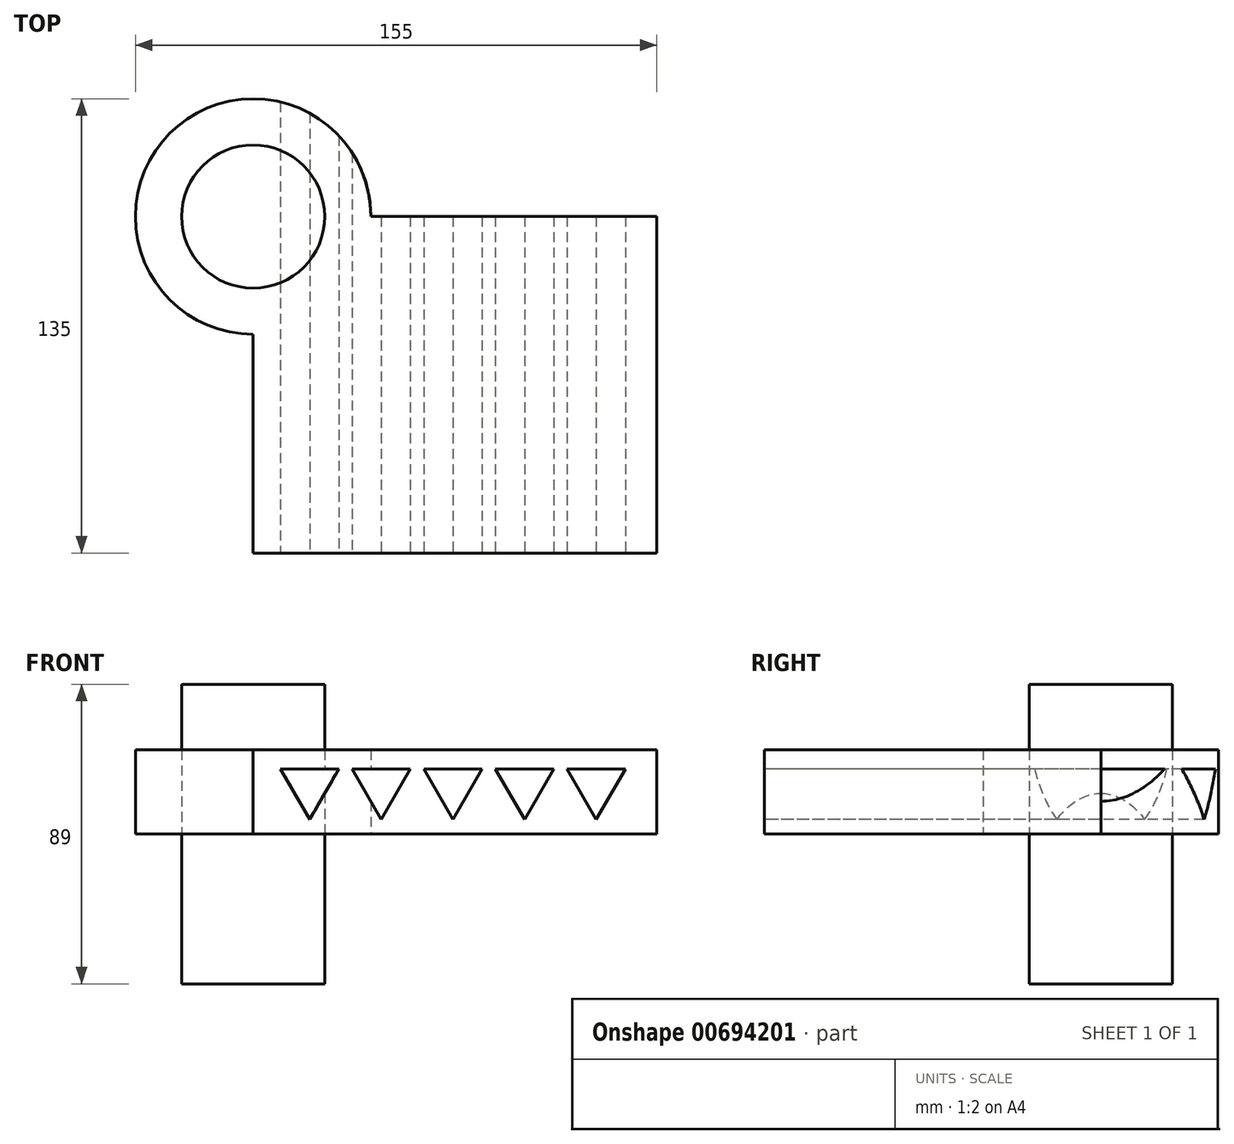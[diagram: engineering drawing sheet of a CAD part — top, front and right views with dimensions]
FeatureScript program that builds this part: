
annotation { "Feature Type Name" : "Feature", "Feature Type Description" : "" }
export const myFeature = defineFeature(function(context is Context, id is Id, definition is map)
    precondition{}
    {
        {
            var Q0;
            Q0=qCreatedBy(makeId("Top.planeOp"),FACE);
            var sketch = newSketch(context, id + "F0", { "sketchPlane" : qUnion([Q0])});
            skLineSegment(sketch, "E0.bottom", {"start": v(60, -50) * mm, "end": v(-60, -50) * mm});
            skLineSegment(sketch, "E0.top", {"start": v(60, 50) * mm, "end": v(-60, 50) * mm});
            skLineSegment(sketch, "E0.left", {"start": v(60, -50) * mm, "end": v(60, 50) * mm});
            skLineSegment(sketch, "E0.right", {"start": v(-60, -50) * mm, "end": v(-60, 50) * mm});
            skPoint(sketch, "E0.middle", {"position": v(0, 0) * mm});
            skCircle(sketch, "E1", {"center": v(-60, 50) * mm, "radius": 35 * mm});
            skArc(sketch, "E2", {"start": v(-41.18, 79.51) * mm, "mid": v(7.3, 57.53) * mm, "end": v(60, 50) * mm});
            skCircle(sketch, "E3", {"center": v(-60, 50) * mm, "radius": 21.28 * mm});
            skSolve(sketch);
        }
        {
            var Q0;
            {var subQ0=sQuery(id+"F0.wireOp",EDGE,"E1");var subQ4=sQuery(id+"F0.wireOp",EDGE,"E0.top");var subQ5=makeQuery(id+"F0.imprint","INTERSECT",VERTEX,{"derivedFrom":[subQ4,subQ0]});Q0=makeQuery(id+"F0.imprint","IMPRINT",FACE,{"disambiguationData":[TD([[makeQuery(id+"F0.imprint","IMPRINT",EDGE,{"disambiguationData":[TD([[subQ5,-1.0]])],"derivedFrom":subQ4}),-1.0]])]});}
            var Q1;
            {var subQ5=sQuery(id+"F0.wireOp",EDGE,"E0.bottom");Q1=makeQuery(id+"F0.imprint","IMPRINT",FACE,{"disambiguationData":[TD([[makeQuery(id+"F0.imprint","IMPRINT",EDGE,{"derivedFrom":subQ5}),-1.0]])]});}
            var Q2;
            {var subQ0=sQuery(id+"F0.wireOp",EDGE,"E1");var subQ1=sQuery(id+"F0.wireOp",EDGE,"E0.top");var subQ2=makeQuery(id+"F0.imprint","INTERSECT",VERTEX,{"derivedFrom":[subQ1,subQ0]});Q2=makeQuery(id+"F0.imprint","IMPRINT",FACE,{"disambiguationData":[TD([[makeQuery(id+"F0.imprint","IMPRINT",EDGE,{"disambiguationData":[TD([[subQ2,-1.0]])],"derivedFrom":subQ1}),1.0]])]});}
            extrude(context, id + "F1", {"entities" : qUnion([Q0, Q1, Q2]), "depth" : 25 * mm, "offsetDistance" : 25 * mm});
        }
        {
            var Q0;
            {var subQ0=sQuery(id+"F0.wireOp",EDGE,"E0.right");var subQ1=sQuery(id+"F0.wireOp",EDGE,"E0.top");var subQ2=makeQuery(id+"F0.imprint","INTERSECT",VERTEX,{"derivedFrom":[subQ1,subQ0]});Q0=makeQuery(id+"F0.imprint","IMPRINT",FACE,{"disambiguationData":[TD([[makeQuery(id+"F0.imprint","IMPRINT",EDGE,{"disambiguationData":[TD([[subQ2,1.0]])],"derivedFrom":subQ1}),-1.0]])]});}
            var Q1;
            {var subQ0=sQuery(id+"F0.wireOp",EDGE,"E0.right");var subQ1=sQuery(id+"F0.wireOp",EDGE,"E0.top");var subQ2=makeQuery(id+"F0.imprint","INTERSECT",VERTEX,{"derivedFrom":[subQ1,subQ0]});Q1=makeQuery(id+"F0.imprint","IMPRINT",FACE,{"disambiguationData":[TD([[makeQuery(id+"F0.imprint","IMPRINT",EDGE,{"disambiguationData":[TD([[subQ2,1.0]])],"derivedFrom":subQ1}),1.0]])]});}
            extrude(context, id + "F2", {"entities" : qUnion([Q0, Q1]), "endBound" : BoundingType.SYMMETRIC, "depth" : 89 * mm, "offsetDistance" : 25 * mm});
        }
        {
            var Q0;
            Q0=makeQuery(id+"F1.opExtrude","SWEPT_FACE",FACE,{"disambiguationData":[OSD([sQuery(id+"F0.wireOp",EDGE,"E0.bottom")])]});
            var sketch = newSketch(context, id + "F3", { "sketchPlane" : qUnion([Q0])});
            skCircle(sketch, "E4.cCircle", {"center": v(-43.2, 14.36) * mm, "radius": 5 * mm, "construction": true});
            skLineSegment(sketch, "E4.0", {"start": v(-34.54, 19.36) * mm, "end": v(-43.2, 4.36) * mm});
            skLineSegment(sketch, "E4.1", {"start": v(-43.2, 4.36) * mm, "end": v(-51.86, 19.36) * mm});
            skLineSegment(sketch, "E4.2", {"start": v(-51.86, 19.36) * mm, "end": v(-34.54, 19.36) * mm});
            skPoint(sketch, "E4.0.midPoint", {"position": v(-38.87, 11.86) * mm});
            skLineSegment(sketch, "E5.1.0.0", {"start": v(-13.24, 19.36) * mm, "end": v(-21.9, 4.36) * mm});
            skLineSegment(sketch, "E5.1.0.1", {"start": v(-30.56, 19.36) * mm, "end": v(-13.24, 19.36) * mm});
            skLineSegment(sketch, "E5.1.0.2", {"start": v(-21.9, 4.36) * mm, "end": v(-30.56, 19.36) * mm});
            skLineSegment(sketch, "E5.2.0.0", {"start": v(8.06, 19.36) * mm, "end": v(-0.6, 4.36) * mm});
            skLineSegment(sketch, "E5.2.0.1", {"start": v(-9.26, 19.36) * mm, "end": v(8.06, 19.36) * mm});
            skLineSegment(sketch, "E5.2.0.2", {"start": v(-0.6, 4.36) * mm, "end": v(-9.26, 19.36) * mm});
            skLineSegment(sketch, "E5.3.0.0", {"start": v(29.36, 19.36) * mm, "end": v(20.7, 4.36) * mm});
            skLineSegment(sketch, "E5.3.0.1", {"start": v(12.04, 19.36) * mm, "end": v(29.36, 19.36) * mm});
            skLineSegment(sketch, "E5.3.0.2", {"start": v(20.7, 4.36) * mm, "end": v(12.04, 19.36) * mm});
            skLineSegment(sketch, "E5.4.0.0", {"start": v(50.66, 19.36) * mm, "end": v(42, 4.36) * mm});
            skLineSegment(sketch, "E5.4.0.1", {"start": v(33.34, 19.36) * mm, "end": v(50.66, 19.36) * mm});
            skLineSegment(sketch, "E5.4.0.2", {"start": v(42, 4.36) * mm, "end": v(33.34, 19.36) * mm});
            skLineSegment(sketch, "E5.direction1", {"start": v(-43.2, 4.36) * mm, "end": v(-21.9, 4.36) * mm, "construction": true});
            skSolve(sketch);
        }
        {
            var Q0;
            Q0=makeQuery(id+"F3.imprint","IMPRINT",FACE,{"disambiguationData":[TD([[makeQuery(id+"F3.imprint","IMPRINT",EDGE,{"derivedFrom":sQuery(id+"F3.wireOp",EDGE,"E4.0")}),-1.0]])]});
            var Q1;
            Q1=makeQuery(id+"F3.imprint","IMPRINT",FACE,{"disambiguationData":[TD([[makeQuery(id+"F3.imprint","IMPRINT",EDGE,{"derivedFrom":sQuery(id+"F3.wireOp",EDGE,"E5.1.0.0")}),-1.0]])]});
            var Q2;
            Q2=makeQuery(id+"F3.imprint","IMPRINT",FACE,{"disambiguationData":[TD([[makeQuery(id+"F3.imprint","IMPRINT",EDGE,{"derivedFrom":sQuery(id+"F3.wireOp",EDGE,"E5.2.0.0")}),-1.0]])]});
            var Q3;
            Q3=makeQuery(id+"F3.imprint","IMPRINT",FACE,{"disambiguationData":[TD([[makeQuery(id+"F3.imprint","IMPRINT",EDGE,{"derivedFrom":sQuery(id+"F3.wireOp",EDGE,"E5.3.0.0")}),-1.0]])]});
            var Q4;
            Q4=makeQuery(id+"F3.imprint","IMPRINT",FACE,{"disambiguationData":[TD([[makeQuery(id+"F3.imprint","IMPRINT",EDGE,{"derivedFrom":sQuery(id+"F3.wireOp",EDGE,"E5.4.0.0")}),-1.0]])]});
            extrude(context, id + "F4", {"entities" : qUnion([Q0, Q1, Q2, Q3, Q4]), "operationType" : NewBodyOperationType.REMOVE, "endBound" : BoundingType.THROUGH_ALL, "oppositeDirection" : true, "depth" : 25 * mm, "offsetDistance" : 25 * mm});
        }
    });
